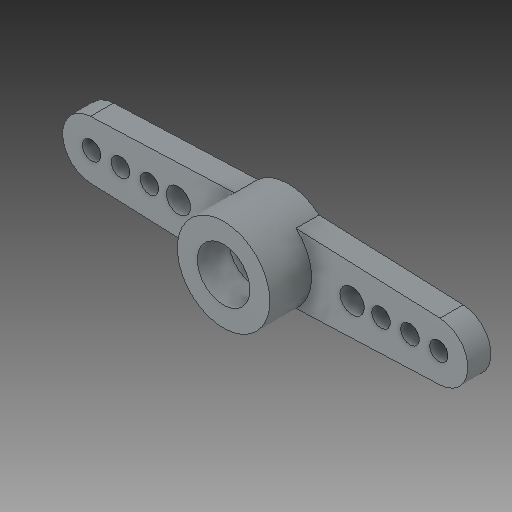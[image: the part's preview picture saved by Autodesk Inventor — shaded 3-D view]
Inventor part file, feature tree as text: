
AUTODESK INVENTOR PART (.ipt)
format: ipt  version: 2018.1 (Build 221171000, 171)  size: 160,768 bytes
history: native  units: mm
features: other x1, extrude x1, sketch x1, imported_body x1
ambient origin geometry x8: Origin, YZ Plane, XZ Plane, XY Plane, X Axis, Y Axis, Z Axis, Center Point
bodies: Body1 (feature_tree)
feature tree (4):
  other  "ソリッド1"
  extrude  "押し出し1"  Depth=7.5mm
  sketch  "スケッチ1"
  imported_body  "Base1"
